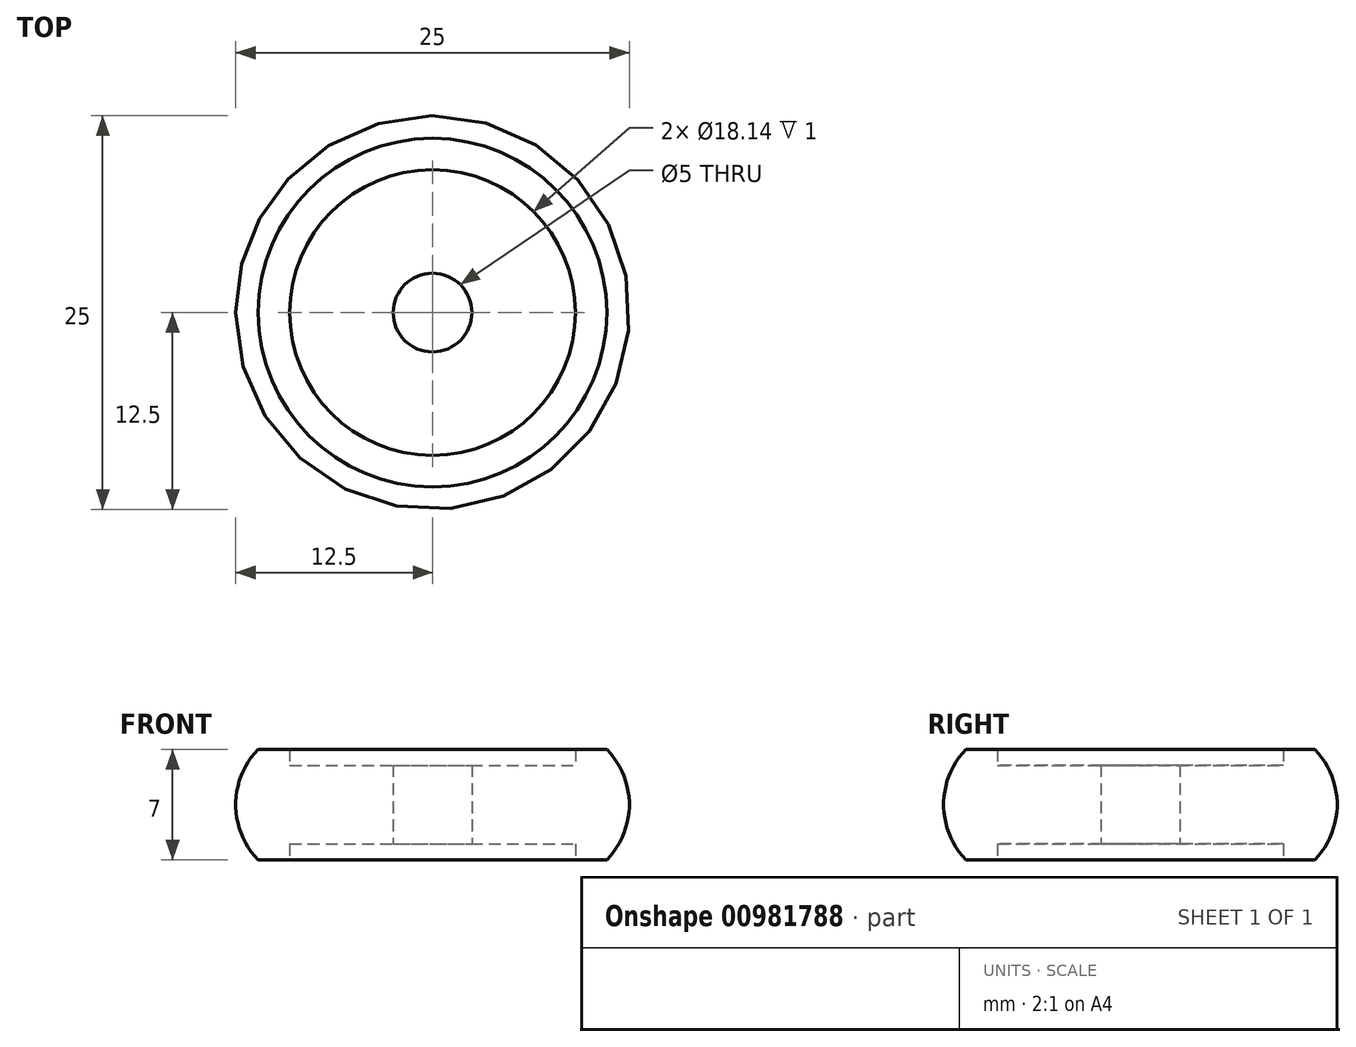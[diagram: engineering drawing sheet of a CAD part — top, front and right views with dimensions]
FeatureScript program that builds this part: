
annotation { "Feature Type Name" : "Feature", "Feature Type Description" : "" }
export const myFeature = defineFeature(function(context is Context, id is Id, definition is map)
    precondition{}
    {
        {
            var Q0;
            Q0=qCreatedBy(makeId("Front.planeOp"),FACE);
            var sketch = newSketch(context, id + "F0", { "sketchPlane" : qUnion([Q0])});
            skLineSegment(sketch, "E0", {"start": v(0, 0) * mm, "end": v(2.5, 0) * mm, "construction": true});
            skArc(sketch, "E1", {"start": v(12.5, 0) * mm, "mid": v(12.13, 1.9) * mm, "end": v(11.07, 3.5) * mm});
            skLineSegment(sketch, "E2", {"start": v(0, 0) * mm, "end": v(0, 8.5) * mm});
            skLineSegment(sketch, "E3", {"start": v(11.07, 3.5) * mm, "end": v(9.07, 3.5) * mm});
            skLineSegment(sketch, "E4", {"start": v(9.07, 3.5) * mm, "end": v(9.07, 2.5) * mm});
            skLineSegment(sketch, "E5", {"start": v(9.07, 2.5) * mm, "end": v(2.5, 2.5) * mm});
            skLineSegment(sketch, "E6", {"start": v(2.5, 2.5) * mm, "end": v(2.5, 0) * mm});
            skLineSegment(sketch, "E7.MirrorCS", {"start": v(2.5, -2.5) * mm, "end": v(2.5, 0) * mm});
            skLineSegment(sketch, "E8.MirrorCS", {"start": v(9.07, -2.5) * mm, "end": v(2.5, -2.5) * mm});
            skLineSegment(sketch, "E9.MirrorCS", {"start": v(9.07, -3.5) * mm, "end": v(9.07, -2.5) * mm});
            skLineSegment(sketch, "E10.MirrorCS", {"start": v(11.07, -3.5) * mm, "end": v(9.07, -3.5) * mm});
            skArc(sketch, "E11.MirrorCS", {"start": v(12.5, 0) * mm, "mid": v(12.13, -1.9) * mm, "end": v(11.07, -3.5) * mm});
            skSolve(sketch);
        }
        {
            var Q0;
            Q0=qSketchRegion(id+"F0",true);
            var Q1;
            Q1=sQuery(id+"F0.wireOp",EDGE,"E2");
            revolve(context, id + "F1", {"surfaceOperationType" : NewSurfaceOperationType.NEW, "entities" : qUnion([Q0]), "axis" : qUnion([Q1]), "revolveType" : RevolveType.FULL});
        }
    });
